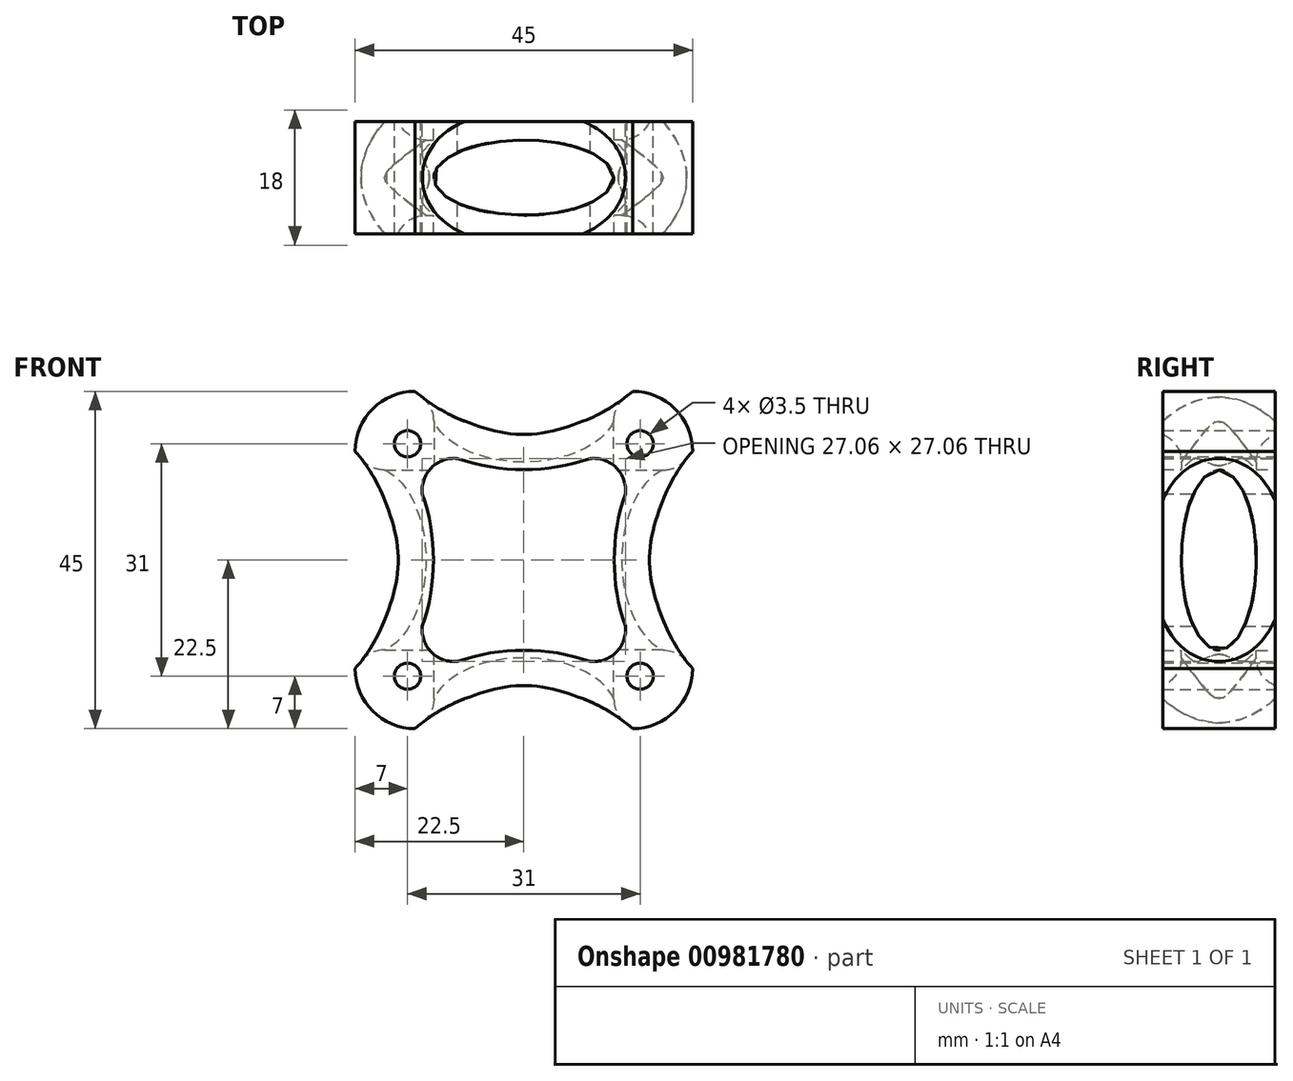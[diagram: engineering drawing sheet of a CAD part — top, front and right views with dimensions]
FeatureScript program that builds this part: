
annotation { "Feature Type Name" : "Feature", "Feature Type Description" : "" }
export const myFeature = defineFeature(function(context is Context, id is Id, definition is map)
    precondition{}
    {
        {
            var Q0;
            Q0=qCreatedBy(makeId("Front.planeOp"),FACE);
            var sketch = newSketch(context, id + "F0", { "sketchPlane" : qUnion([Q0])});
            skLineSegment(sketch, "E0.bottom", {"start": v(-15.5, 15.5) * mm, "end": v(15.5, 15.5) * mm, "construction": true});
            skLineSegment(sketch, "E0.top", {"start": v(-15.5, -15.5) * mm, "end": v(15.5, -15.5) * mm, "construction": true});
            skLineSegment(sketch, "E0.left", {"start": v(-15.5, 15.5) * mm, "end": v(-15.5, -15.5) * mm, "construction": true});
            skLineSegment(sketch, "E0.right", {"start": v(15.5, 15.5) * mm, "end": v(15.5, -15.5) * mm, "construction": true});
            skPoint(sketch, "E0.middle", {"position": v(0, 0) * mm});
            skCircle(sketch, "E1", {"center": v(-15.5, 15.5) * mm, "radius": 2.75 * mm, "construction": true});
            skCircle(sketch, "E2", {"center": v(15.5, 15.5) * mm, "radius": 2.75 * mm, "construction": true});
            skCircle(sketch, "E3", {"center": v(-15.5, -15.5) * mm, "radius": 2.75 * mm, "construction": true});
            skCircle(sketch, "E4", {"center": v(15.5, -15.5) * mm, "radius": 2.75 * mm, "construction": true});
            skCircle(sketch, "E5", {"center": v(0, 0) * mm, "radius": 6.6 * mm});
            skLineSegment(sketch, "E6.bottom", {"start": v(14.5, 22.5) * mm, "end": v(-14.5, 22.5) * mm});
            skLineSegment(sketch, "E6.top", {"start": v(14.5, -22.5) * mm, "end": v(-14.5, -22.5) * mm});
            skLineSegment(sketch, "E6.left", {"start": v(22.5, 14.5) * mm, "end": v(22.5, 0) * mm});
            skLineSegment(sketch, "E6.right", {"start": v(-22.5, 14.5) * mm, "end": v(-22.5, 0) * mm});
            skPoint(sketch, "E7.visualSharp", {"position": v(-22.5, 22.5) * mm});
            skArc(sketch, "E7.filletArc", {"start": v(-14.5, 22.5) * mm, "mid": v(-20.16, 20.16) * mm, "end": v(-22.5, 14.5) * mm});
            skPoint(sketch, "E8.visualSharp", {"position": v(22.5, 22.5) * mm});
            skArc(sketch, "E8.filletArc", {"start": v(22.5, 14.5) * mm, "mid": v(20.16, 20.16) * mm, "end": v(14.5, 22.5) * mm});
            skPoint(sketch, "E9.visualSharp", {"position": v(22.5, -22.5) * mm});
            skArc(sketch, "E9.filletArc", {"start": v(14.5, -22.5) * mm, "mid": v(20.16, -20.16) * mm, "end": v(22.5, -14.5) * mm});
            skPoint(sketch, "E10.visualSharp", {"position": v(-22.5, -22.5) * mm});
            skArc(sketch, "E10.filletArc", {"start": v(-22.5, -14.5) * mm, "mid": v(-20.16, -20.16) * mm, "end": v(-14.5, -22.5) * mm});
            skLineSegment(sketch, "E11", {"start": v(-22.5, 0) * mm, "end": v(-22.5, -14.5) * mm});
            skLineSegment(sketch, "E12", {"start": v(22.5, 0) * mm, "end": v(22.5, -14.5) * mm});
            skArc(sketch, "E13", {"start": v(-22.5, -14.5) * mm, "mid": v(-17.05, 0) * mm, "end": v(-22.5, 14.5) * mm});
            skArc(sketch, "E14", {"start": v(-14.5, 22.5) * mm, "mid": v(0, 17.05) * mm, "end": v(14.5, 22.5) * mm});
            skArc(sketch, "E15", {"start": v(22.5, 14.5) * mm, "mid": v(17.05, 0) * mm, "end": v(22.5, -14.5) * mm});
            skArc(sketch, "E16", {"start": v(14.5, -22.5) * mm, "mid": v(0, -17.05) * mm, "end": v(-14.5, -22.5) * mm});
            skArc(sketch, "E17", {"start": v(-8.83, 13.53) * mm, "mid": v(0, 12.05) * mm, "end": v(8.83, 13.53) * mm});
            skArc(sketch, "E18", {"start": v(-8.83, 13.53) * mm, "mid": v(-12.3, 12.3) * mm, "end": v(-13.53, 8.83) * mm});
            skArc(sketch, "E19.1.0", {"start": v(-13.53, -8.83) * mm, "mid": v(-12.3, -12.3) * mm, "end": v(-8.83, -13.53) * mm});
            skArc(sketch, "E19.2.0", {"start": v(8.83, -13.53) * mm, "mid": v(12.3, -12.3) * mm, "end": v(13.53, -8.83) * mm});
            skArc(sketch, "E19.3.0", {"start": v(13.53, 8.83) * mm, "mid": v(12.3, 12.3) * mm, "end": v(8.83, 13.53) * mm});
            skArc(sketch, "E20", {"start": v(13.53, 8.83) * mm, "mid": v(12.05, 0) * mm, "end": v(13.53, -8.83) * mm});
            skArc(sketch, "E21", {"start": v(8.83, -13.53) * mm, "mid": v(0, -12.05) * mm, "end": v(-8.83, -13.53) * mm});
            skArc(sketch, "E22", {"start": v(-13.53, -8.83) * mm, "mid": v(-12.05, 0) * mm, "end": v(-13.53, 8.83) * mm});
            skSolve(sketch);
        }
        {
            var Q0;
            Q0=makeQuery(id+"F0.imprint","IMPRINT",FACE,{"disambiguationData":[TD([[makeQuery(id+"F0.imprint","IMPRINT",EDGE,{"derivedFrom":sQuery(id+"F0.wireOp",EDGE,"E7.filletArc")}),1.0]])]});
            extrude(context, id + "F1", {"entities" : qUnion([Q0]), "depth" : 15 * mm, "offsetDistance" : 25 * mm});
        }
        {
            var Q0;
            Q0=sQuery(id+"F0.wireOp",VERTEX,"E0.bottom.end");
            var Q1;
            Q1=sQuery(id+"F0.wireOp",VERTEX,"E0.top.end");
            var Q2;
            Q2=sQuery(id+"F0.wireOp",VERTEX,"E0.top.start");
            var Q3;
            Q3=sQuery(id+"F0.wireOp",VERTEX,"E0.bottom.start");
            var Q4;
            Q4=makeQuery(id+"F1.opExtrude","SWEPT_BODY",BODY,{"disambiguationData":[OSD([sQuery(id+"F0.wireOp",EDGE,"E7.filletArc"),sQuery(id+"F0.wireOp",EDGE,"E8.filletArc"),sQuery(id+"F0.wireOp",EDGE,"E9.filletArc"),sQuery(id+"F0.wireOp",EDGE,"E10.filletArc"),sQuery(id+"F0.wireOp",EDGE,"E13"),sQuery(id+"F0.wireOp",EDGE,"E14"),sQuery(id+"F0.wireOp",EDGE,"E15"),sQuery(id+"F0.wireOp",EDGE,"E16"),sQuery(id+"F0.wireOp",EDGE,"E17"),sQuery(id+"F0.wireOp",EDGE,"E18"),sQuery(id+"F0.wireOp",EDGE,"E19.1.0"),sQuery(id+"F0.wireOp",EDGE,"E19.2.0"),sQuery(id+"F0.wireOp",EDGE,"E19.3.0"),sQuery(id+"F0.wireOp",EDGE,"E20"),sQuery(id+"F0.wireOp",EDGE,"E21"),sQuery(id+"F0.wireOp",EDGE,"E22")])]});
            hole(context, id + "F2", {"style" : HoleStyle.SIMPLE, "endStyle" : HoleEndStyle.THROUGH, "oppositeDirection" : true, "holeDiameter" : 3.5 * mm, "majorDiameter" : 5 * mm, "isTappedThrough" : true, "tappedDepth" : 12 * mm, "tapClearance" : 3, "locations" : qUnion([Q0, Q1, Q2, Q3]), "scope" : qUnion([Q4])});
        }
        {
            var Q0;
            Q0=qCreatedBy(makeId("Right.planeOp"),FACE);
            cPlane(context, id + "F3", {"entities" : qUnion([Q0]), "cplaneType" : CPlaneType.OFFSET, "offset" : 25 * mm, "width" : 150 * mm, "height" : 150 * mm});
        }
        {
            var Q0;
            Q0=qCreatedBy(makeId("Top.planeOp"),FACE);
            cPlane(context, id + "F4", {"entities" : qUnion([Q0]), "cplaneType" : CPlaneType.OFFSET, "offset" : 25 * mm, "width" : 150 * mm, "height" : 150 * mm});
        }
        {
            var Q0;
            Q0=qCreatedBy(id+"F3.planeOp",FACE);
            var sketch = newSketch(context, id + "F5", { "sketchPlane" : qUnion([Q0])});
            skLineSegment(sketch, "E23", {"start": v(0, 0) * mm, "end": v(-15, 0) * mm});
            skEllipse(sketch, "E24", {"center": v(-7.5, 0) * mm, "majorRadius": 12 * mm, "minorRadius": 5 * mm, "majorAxis": v(0, 1)});
            skSolve(sketch);
        }
        {
            var Q0;
            Q0=qSketchRegion(id+"F5",true);
            extrude(context, id + "F6", {"entities" : qUnion([Q0]), "operationType" : NewBodyOperationType.REMOVE, "oppositeDirection" : true, "depth" : 60 * mm, "offsetDistance" : 25 * mm});
        }
        {
            var Q0;
            Q0=qCreatedBy(id+"F4.planeOp",FACE);
            var sketch = newSketch(context, id + "F7", { "sketchPlane" : qUnion([Q0])});
            skEllipse(sketch, "E25", {"center": v(0, -7.5) * mm, "majorRadius": 12 * mm, "minorRadius": 5 * mm, "majorAxis": v(1, 0)});
            skSolve(sketch);
        }
        {
            var Q0;
            Q0=makeQuery(id+"F7.imprint","IMPRINT",FACE,{"disambiguationData":[TD([[makeQuery(id+"F7.imprint","IMPRINT",EDGE,{"derivedFrom":sQuery(id+"F7.wireOp",EDGE,"E25")}),1.0]])]});
            extrude(context, id + "F8", {"entities" : qUnion([Q0]), "operationType" : NewBodyOperationType.REMOVE, "oppositeDirection" : true, "depth" : 60 * mm, "offsetDistance" : 25 * mm});
        }
        {
            var Q0;
            Q0=makeQuery(id+"F6.boolean.opBoolean","INTERSECT",EDGE,{"derivedFrom":[makeQuery(id+"F1.opExtrude","SWEPT_FACE",FACE,{"disambiguationData":[OSD([sQuery(id+"F0.wireOp",EDGE,"E15")])]}),makeQuery(id+"F6.opExtrude","SWEPT_FACE",FACE,{"disambiguationData":[OSD([sQuery(id+"F5.wireOp",EDGE,"E24")])]})]});
            var Q1;
            Q1=makeQuery(id+"F8.boolean.opBoolean","INTERSECT",EDGE,{"derivedFrom":[makeQuery(id+"F1.opExtrude","SWEPT_FACE",FACE,{"disambiguationData":[OSD([sQuery(id+"F0.wireOp",EDGE,"E16")])]}),makeQuery(id+"F8.opExtrude","SWEPT_FACE",FACE,{"disambiguationData":[OSD([sQuery(id+"F7.wireOp",EDGE,"E25")])]})]});
            var Q2;
            Q2=makeQuery(id+"F6.boolean.opBoolean","INTERSECT",EDGE,{"derivedFrom":[makeQuery(id+"F1.opExtrude","SWEPT_FACE",FACE,{"disambiguationData":[OSD([sQuery(id+"F0.wireOp",EDGE,"E13")])]}),makeQuery(id+"F6.opExtrude","SWEPT_FACE",FACE,{"disambiguationData":[OSD([sQuery(id+"F5.wireOp",EDGE,"E24")])]})]});
            var Q3;
            Q3=makeQuery(id+"F8.boolean.opBoolean","INTERSECT",EDGE,{"derivedFrom":[makeQuery(id+"F1.opExtrude","SWEPT_FACE",FACE,{"disambiguationData":[OSD([sQuery(id+"F0.wireOp",EDGE,"E14")])]}),makeQuery(id+"F8.opExtrude","SWEPT_FACE",FACE,{"disambiguationData":[OSD([sQuery(id+"F7.wireOp",EDGE,"E25")])]})]});
            fillet(context, id + "F9", {"entities" : qUnion([Q0, Q1, Q2, Q3]), "radius" : 4 * mm, "tangentPropagation" : true, "allowEdgeOverflow" : false});
        }
    });
